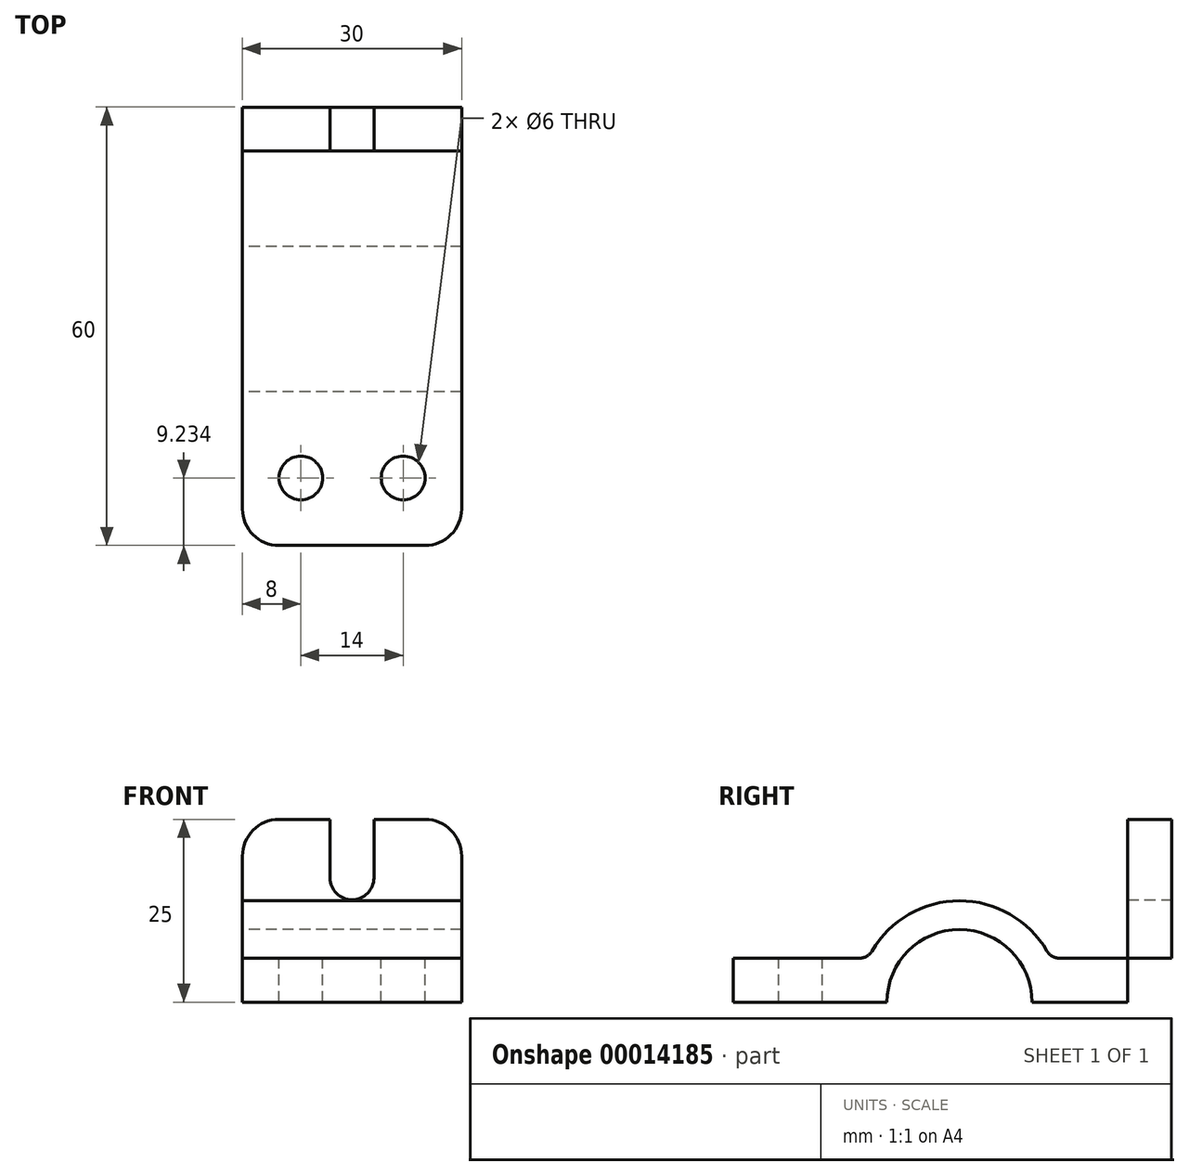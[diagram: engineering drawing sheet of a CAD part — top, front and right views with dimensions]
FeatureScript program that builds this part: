
annotation { "Feature Type Name" : "Feature", "Feature Type Description" : "" }
export const myFeature = defineFeature(function(context is Context, id is Id, definition is map)
    precondition{}
    {
        {
            var Q0;
            Q0=qCreatedBy(makeId("Right.planeOp"),FACE);
            var sketch = newSketch(context, id + "F0", { "sketchPlane" : qUnion([Q0])});
            skCircle(sketch, "E0", {"center": v(0, 0) * mm, "radius": 13.87 * mm});
            skCircle(sketch, "E1", {"center": v(0, 0) * mm, "radius": 9.93 * mm});
            skLineSegment(sketch, "E2.bottom", {"start": v(-30.98, 6) * mm, "end": v(29.02, 6) * mm});
            skLineSegment(sketch, "E2.top", {"start": v(-30.98, 0) * mm, "end": v(29.02, 0) * mm});
            skLineSegment(sketch, "E2.left", {"start": v(-30.98, 6) * mm, "end": v(-30.98, 0) * mm});
            skLineSegment(sketch, "E2.right", {"start": v(29.02, 6) * mm, "end": v(29.02, 0) * mm});
            skLineSegment(sketch, "E3.bottom", {"start": v(29.02, 0) * mm, "end": v(23.02, 0) * mm});
            skLineSegment(sketch, "E3.top", {"start": v(29.02, 25) * mm, "end": v(23.02, 25) * mm});
            skLineSegment(sketch, "E3.left", {"start": v(29.02, 0) * mm, "end": v(29.02, 25) * mm});
            skLineSegment(sketch, "E3.right", {"start": v(23.02, 0) * mm, "end": v(23.02, 25) * mm});
            skSolve(sketch);
        }
        {
            var Q0;
            {var subQ0=sQuery(id+"F0.wireOp",EDGE,"E2.left");Q0=makeQuery(id+"F0.imprint","IMPRINT",FACE,{"disambiguationData":[TD([[makeQuery(id+"F0.imprint","IMPRINT",EDGE,{"derivedFrom":subQ0}),1.0]])]});}
            var Q1;
            {var subQ3=sQuery(id+"F0.wireOp",EDGE,"E0");var subQ5=sQuery(id+"F0.wireOp",EDGE,"E2.bottom");var subQ7=makeQuery(id+"F0.imprint","INTERSECT",VERTEX,{"disambiguationData":[OD(1.0)],"derivedFrom":[subQ3,subQ5]});Q1=makeQuery(id+"F0.imprint","IMPRINT",FACE,{"disambiguationData":[TD([[makeQuery(id+"F0.imprint","IMPRINT",EDGE,{"disambiguationData":[TD([[subQ7,-1.0]])],"derivedFrom":subQ3}),1.0]])]});}
            var Q2;
            {var subQ0=sQuery(id+"F0.wireOp",EDGE,"E2.bottom");var subQ3=sQuery(id+"F0.wireOp",EDGE,"E0");var subQ4=makeQuery(id+"F0.imprint","INTERSECT",VERTEX,{"disambiguationData":[OD(0.0)],"derivedFrom":[subQ3,subQ0]});Q2=makeQuery(id+"F0.imprint","IMPRINT",FACE,{"disambiguationData":[TD([[makeQuery(id+"F0.imprint","IMPRINT",EDGE,{"disambiguationData":[TD([[subQ4,-1.0]])],"derivedFrom":subQ3}),1.0]])]});}
            var Q3;
            {var subQ3=sQuery(id+"F0.wireOp",EDGE,"E0");var subQ5=sQuery(id+"F0.wireOp",EDGE,"E2.bottom");var subQ7=makeQuery(id+"F0.imprint","INTERSECT",VERTEX,{"disambiguationData":[OD(0.0)],"derivedFrom":[subQ3,subQ5]});Q3=makeQuery(id+"F0.imprint","IMPRINT",FACE,{"disambiguationData":[TD([[makeQuery(id+"F0.imprint","IMPRINT",EDGE,{"disambiguationData":[TD([[subQ7,1.0]])],"derivedFrom":subQ3}),1.0]])]});}
            var Q4;
            {var subQ1=sQuery(id+"F0.wireOp",EDGE,"E2.bottom");var subQ5=sQuery(id+"F0.wireOp",EDGE,"E0");var subQ7=makeQuery(id+"F0.imprint","INTERSECT",VERTEX,{"disambiguationData":[OD(0.0)],"derivedFrom":[subQ5,subQ1]});Q4=makeQuery(id+"F0.imprint","IMPRINT",FACE,{"disambiguationData":[TD([[makeQuery(id+"F0.imprint","IMPRINT",EDGE,{"disambiguationData":[TD([[subQ7,1.0]])],"derivedFrom":subQ5}),-1.0]])]});}
            var Q5;
            {var subQ3=sQuery(id+"F0.wireOp",EDGE,"E3.top");Q5=makeQuery(id+"F0.imprint","IMPRINT",FACE,{"disambiguationData":[TD([[makeQuery(id+"F0.imprint","IMPRINT",EDGE,{"derivedFrom":subQ3}),1.0]])]});}
            var Q6;
            {var subQ3=sQuery(id+"F0.wireOp",EDGE,"E3.bottom");Q6=makeQuery(id+"F0.imprint","IMPRINT",FACE,{"disambiguationData":[TD([[makeQuery(id+"F0.imprint","IMPRINT",EDGE,{"derivedFrom":subQ3}),-1.0]])]});}
            extrude(context, id + "F1", {"entities" : qUnion([Q0, Q1, Q2, Q3, Q4, Q5, Q6]), "endBound" : BoundingType.SYMMETRIC, "depth" : 30 * mm});
        }
        {
            var Q0;
            Q0=makeQuery(id+"F1.opExtrude","SWEPT_FACE",FACE,{"disambiguationData":[OSD([sQuery(id+"F0.wireOp",EDGE,"E3.left")])]});
            var sketch = newSketch(context, id + "F2", { "sketchPlane" : qUnion([Q0])});
            skLineSegment(sketch, "E4", {"start": v(0, 0) * mm, "end": v(0, 25) * mm, "construction": true});
            skCircle(sketch, "E5", {"center": v(0, 17) * mm, "radius": 3 * mm});
            skLineSegment(sketch, "E6", {"start": v(-3, 17) * mm, "end": v(-3, 25) * mm});
            skLineSegment(sketch, "E7", {"start": v(3, 17) * mm, "end": v(3, 25) * mm});
            skSolve(sketch);
        }
        {
            var Q0;
            {var subQ0=sQuery(id+"F2.wireOp",EDGE,"E5");var subQ2=makeQuery(id+"F2.imprint","INTERSECT",VERTEX,{"derivedFrom":[subQ0,sQuery(id+"F2.wireOp",EDGE,"E6")]});Q0=makeQuery(id+"F2.imprint","IMPRINT",FACE,{"disambiguationData":[TD([[makeQuery(id+"F2.imprint","IMPRINT",EDGE,{"disambiguationData":[TD([[subQ2,1.0]])],"derivedFrom":subQ0}),1.0]])]});}
            var Q1;
            {var subQ2=sQuery(id+"F2.wireOp",EDGE,"E6");Q1=makeQuery(id+"F2.imprint","IMPRINT",FACE,{"disambiguationData":[TD([[makeQuery(id+"F2.imprint","IMPRINT",EDGE,{"derivedFrom":subQ2}),-1.0]])]});}
            extrude(context, id + "F3", {"entities" : qUnion([Q0, Q1]), "operationType" : NewBodyOperationType.REMOVE, "oppositeDirection" : true, "depth" : 25 * mm});
        }
        {
            var Q0;
            {var subQ0=sQuery(id+"F0.wireOp",EDGE,"E2.bottom");Q0=makeQuery(id+"F1.opExtrude","SWEPT_FACE",FACE,{"disambiguationData":[OSD([subQ0]),TDD([makeQuery(id+"F0.imprint","IMPRINT",EDGE,{"disambiguationData":[TD([[makeQuery(id+"F0.imprint","INTERSECT",VERTEX,{"derivedFrom":[subQ0,sQuery(id+"F0.wireOp",EDGE,"E2.left")]}),-1.0]])],"derivedFrom":subQ0})])]});}
            var sketch = newSketch(context, id + "F4", { "sketchPlane" : qUnion([Q0])});
            skLineSegment(sketch, "E8", {"start": v(-15, -21.75) * mm, "end": v(15, -21.75) * mm, "construction": true});
            skCircle(sketch, "E9", {"center": v(-7, -21.75) * mm, "radius": 3 * mm});
            skCircle(sketch, "E10", {"center": v(7, -21.75) * mm, "radius": 3 * mm});
            skSolve(sketch);
        }
        {
            var Q0;
            Q0=makeQuery(id+"F4.imprint","IMPRINT",FACE,{"disambiguationData":[TD([[makeQuery(id+"F4.imprint","IMPRINT",EDGE,{"derivedFrom":sQuery(id+"F4.wireOp",EDGE,"E9")}),1.0]])]});
            var Q1;
            Q1=makeQuery(id+"F4.imprint","IMPRINT",FACE,{"disambiguationData":[TD([[makeQuery(id+"F4.imprint","IMPRINT",EDGE,{"derivedFrom":sQuery(id+"F4.wireOp",EDGE,"E10")}),1.0]])]});
            extrude(context, id + "F5", {"entities" : qUnion([Q0, Q1]), "operationType" : NewBodyOperationType.REMOVE, "endBound" : BoundingType.THROUGH_ALL, "oppositeDirection" : true, "depth" : 25 * mm});
        }
        {
            var Q0;
            Q0=makeQuery(id+"F1.opExtrude","CAP_EDGE",EDGE,{"disambiguationData":[OSD([sQuery(id+"F0.wireOp",EDGE,"E2.left")])],"isStart":true});
            var Q1;
            Q1=makeQuery(id+"F1.opExtrude","CAP_EDGE",EDGE,{"disambiguationData":[OSD([sQuery(id+"F0.wireOp",EDGE,"E2.left")])],"isStart":false});
            var Q2;
            Q2=makeQuery(id+"F1.opExtrude","CAP_EDGE",EDGE,{"disambiguationData":[OSD([sQuery(id+"F0.wireOp",EDGE,"E3.top")])],"isStart":false});
            var Q3;
            Q3=makeQuery(id+"F1.opExtrude","CAP_EDGE",EDGE,{"disambiguationData":[OSD([sQuery(id+"F0.wireOp",EDGE,"E3.top")])],"isStart":true});
            fillet(context, id + "F6", {"entities" : qUnion([Q0, Q1, Q2, Q3]), "radius" : 5 * mm, "tangentPropagation" : true, "allowEdgeOverflow" : false});
        }
        {
            var Q0;
            {var subQ0=sQuery(id+"F0.wireOp",EDGE,"E0");var subQ1=sQuery(id+"F0.wireOp",EDGE,"E2.bottom");Q0=makeQuery(id+"F1.opExtrude","SWEPT_EDGE",EDGE,{"disambiguationData":[OSD([subQ0,subQ1]),TDD([makeQuery(id+"F0.imprint","INTERSECT",VERTEX,{"disambiguationData":[OD(1.0)],"derivedFrom":[subQ0,subQ1]})])]});}
            var Q1;
            {var subQ0=sQuery(id+"F0.wireOp",EDGE,"E0");var subQ1=sQuery(id+"F0.wireOp",EDGE,"E2.bottom");Q1=makeQuery(id+"F1.opExtrude","SWEPT_EDGE",EDGE,{"disambiguationData":[OSD([subQ0,subQ1]),TDD([makeQuery(id+"F0.imprint","INTERSECT",VERTEX,{"disambiguationData":[OD(0.0)],"derivedFrom":[subQ0,subQ1]})])]});}
            fillet(context, id + "F7", {"entities" : qUnion([Q0, Q1]), "radius" : 2 * mm, "tangentPropagation" : true, "allowEdgeOverflow" : false});
        }
    });
